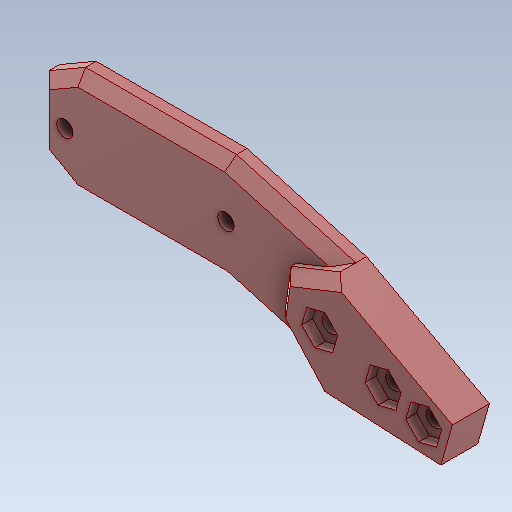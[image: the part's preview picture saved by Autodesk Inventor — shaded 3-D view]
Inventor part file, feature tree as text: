
AUTODESK INVENTOR PART (.ipt)
format: ipt  version: 2020 (Build 240168000, 168)  size: 194,560 bytes
history: native  units: in
note: dims shown in document units (in); Inventor stores cm internally (conversion verified against a paired STEP export)
features: sketch x4, other x3, extrude x1
ambient origin geometry x8: Origin, YZ Plane, XZ Plane, XY Plane, X Axis, Y Axis, Z Axis, Center Point
bodies: Solid1 (feature_tree)
feature tree (8):
  other  "Fibula.ipt"
  extrude  "Extrusion1"  Depth=0.2756in
  other  "Solid1::Fibula.ipt"
  other  "TaggingFeature1"
  sketch  "Sketch1"  dims[d0=0.3937in d1=0.2756in]
  sketch  "Sketch3"  dims[d2=0.2756in]
  sketch  "Sketch4"  dims[d4=0.3937in d5=0.0in]
  sketch  "Sketch5"  dims[d6=0.2756in]
